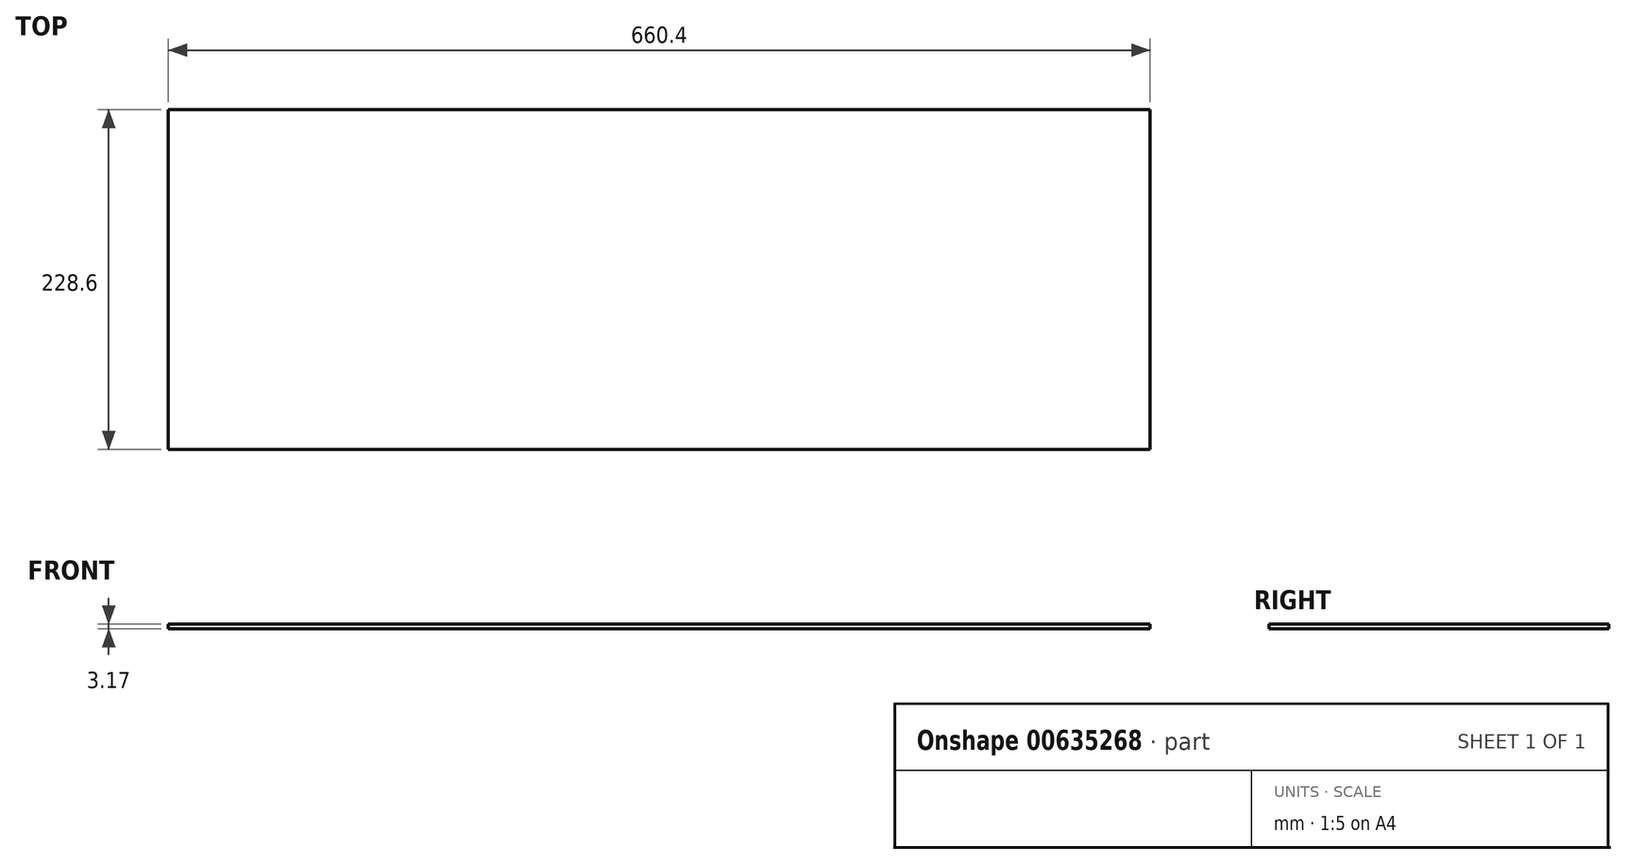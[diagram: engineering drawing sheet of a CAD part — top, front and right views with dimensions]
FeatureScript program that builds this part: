
annotation { "Feature Type Name" : "Feature", "Feature Type Description" : "" }
export const myFeature = defineFeature(function(context is Context, id is Id, definition is map)
    precondition{}
    {
        {
            var Q0;
            Q0=qCreatedBy(makeId("Top.planeOp"),FACE);
            var sketch = newSketch(context, id + "F0", { "sketchPlane" : qUnion([Q0])});
            skLineSegment(sketch, "E0.bottom", {"start": v(330.2, 114.3) * mm, "end": v(-330.2, 114.3) * mm});
            skLineSegment(sketch, "E0.top", {"start": v(330.2, -114.3) * mm, "end": v(-330.2, -114.3) * mm});
            skLineSegment(sketch, "E0.left", {"start": v(330.2, 114.3) * mm, "end": v(330.2, -114.3) * mm});
            skLineSegment(sketch, "E0.right", {"start": v(-330.2, 114.3) * mm, "end": v(-330.2, -114.3) * mm});
            skPoint(sketch, "E0.middle", {"position": v(0, 0) * mm});
            skSolve(sketch);
        }
        {
            var Q0;
            Q0 = qSketchRegion(id + "F0", true);
            extrude(context, id + "F1", {"entities" : qUnion([Q0]), "depth" : 3.17 * mm, "offsetDistance" : 25.4 * mm});
        }
    });
